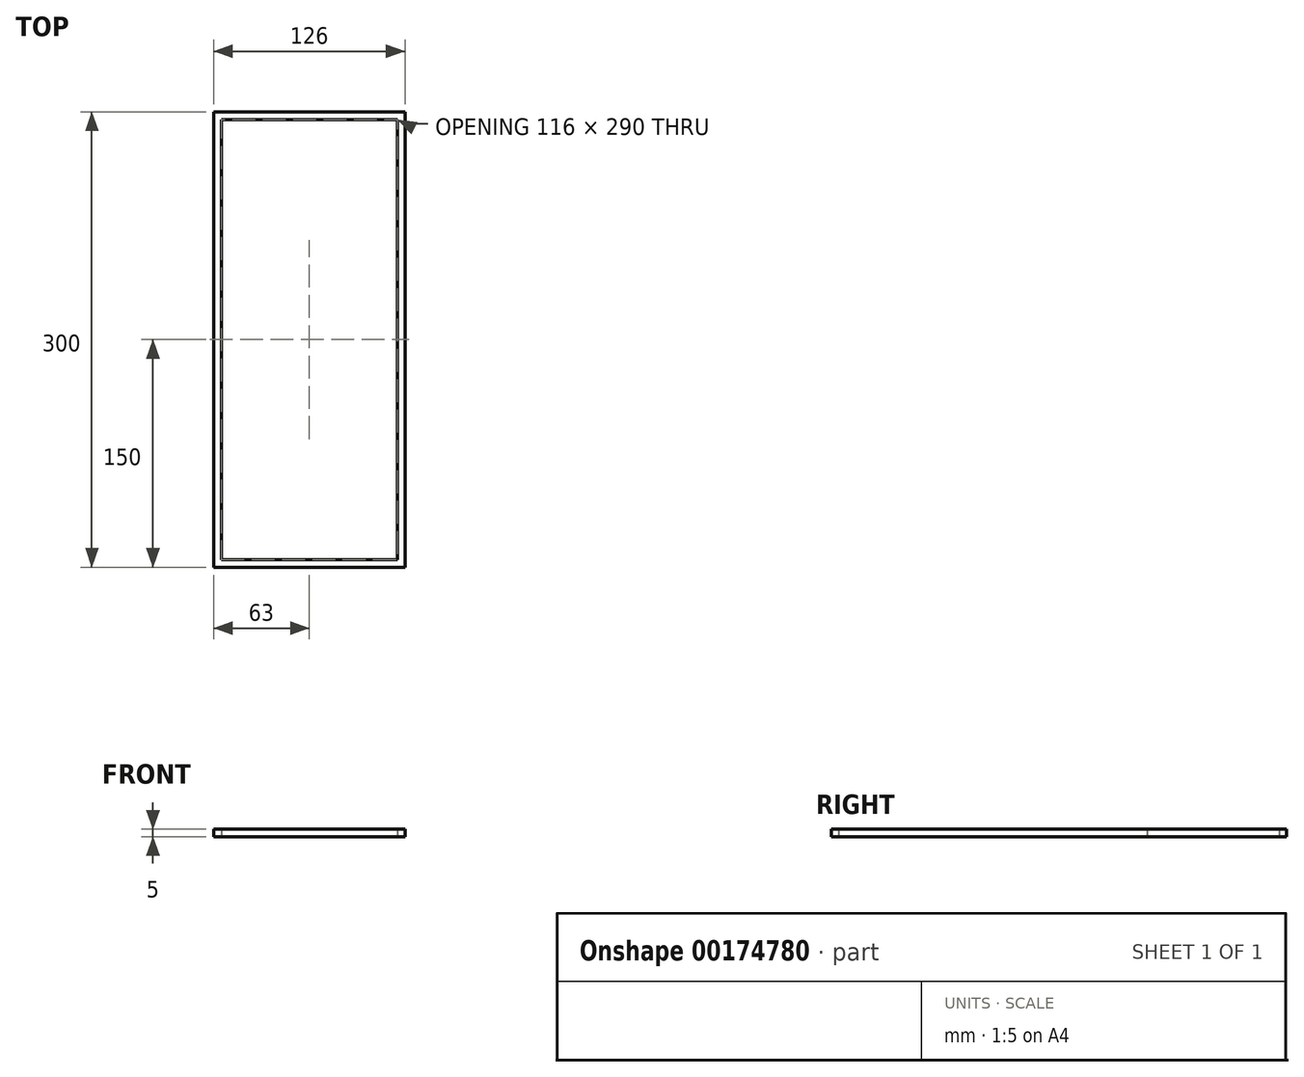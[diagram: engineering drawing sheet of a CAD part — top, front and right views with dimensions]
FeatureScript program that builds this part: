
annotation { "Feature Type Name" : "Feature", "Feature Type Description" : "" }
export const myFeature = defineFeature(function(context is Context, id is Id, definition is map)
    precondition{}
    {
        {
            var Q0;
            Q0=qCreatedBy(makeId("Top.planeOp"),FACE);
            var sketch = newSketch(context, id + "F0", { "sketchPlane" : qUnion([Q0])});
            skLineSegment(sketch, "E0.bottom", {"start": v(0, 0) * mm, "end": v(126, 0) * mm});
            skLineSegment(sketch, "E0.top", {"start": v(0, 300) * mm, "end": v(126, 300) * mm});
            skLineSegment(sketch, "E0.left", {"start": v(0, 0) * mm, "end": v(0, 300) * mm});
            skLineSegment(sketch, "E0.right", {"start": v(126, 0) * mm, "end": v(126, 300) * mm});
            skLineSegment(sketch, "E1.bottom", {"start": v(5, 5) * mm, "end": v(34, 5) * mm});
            skLineSegment(sketch, "E1.top", {"start": v(5, 34) * mm, "end": v(34, 34) * mm});
            skLineSegment(sketch, "E1.left", {"start": v(5, 5) * mm, "end": v(5, 34) * mm});
            skLineSegment(sketch, "E1.right", {"start": v(34, 5) * mm, "end": v(34, 34) * mm});
            skLineSegment(sketch, "E2.0.1.0", {"start": v(5, 63) * mm, "end": v(34, 63) * mm});
            skLineSegment(sketch, "E2.0.1.1", {"start": v(5, 34) * mm, "end": v(5, 63) * mm});
            skLineSegment(sketch, "E2.0.2.0", {"start": v(5, 92) * mm, "end": v(34, 92) * mm});
            skLineSegment(sketch, "E2.0.2.1", {"start": v(5, 63) * mm, "end": v(5, 92) * mm});
            skLineSegment(sketch, "E2.0.3.0", {"start": v(5, 121) * mm, "end": v(34, 121) * mm});
            skLineSegment(sketch, "E2.0.3.1", {"start": v(5, 92) * mm, "end": v(5, 121) * mm});
            skLineSegment(sketch, "E2.0.4.0", {"start": v(5, 150) * mm, "end": v(34, 150) * mm});
            skLineSegment(sketch, "E2.0.4.1", {"start": v(5, 121) * mm, "end": v(5, 150) * mm});
            skLineSegment(sketch, "E2.0.5.0", {"start": v(5, 179) * mm, "end": v(34, 179) * mm});
            skLineSegment(sketch, "E2.0.5.1", {"start": v(5, 150) * mm, "end": v(5, 179) * mm});
            skLineSegment(sketch, "E2.0.6.0", {"start": v(5, 208) * mm, "end": v(34, 208) * mm});
            skLineSegment(sketch, "E2.0.6.1", {"start": v(5, 179) * mm, "end": v(5, 208) * mm});
            skLineSegment(sketch, "E2.0.7.0", {"start": v(5, 237) * mm, "end": v(34, 237) * mm});
            skLineSegment(sketch, "E2.0.7.1", {"start": v(5, 208) * mm, "end": v(5, 237) * mm});
            skLineSegment(sketch, "E2.0.8.0", {"start": v(5, 266) * mm, "end": v(34, 266) * mm});
            skLineSegment(sketch, "E2.0.8.1", {"start": v(5, 237) * mm, "end": v(5, 266) * mm});
            skLineSegment(sketch, "E2.0.9.0", {"start": v(5, 295) * mm, "end": v(34, 295) * mm});
            skLineSegment(sketch, "E2.0.9.1", {"start": v(5, 266) * mm, "end": v(5, 295) * mm});
            skLineSegment(sketch, "E2.1.0.0", {"start": v(34, 34) * mm, "end": v(63, 34) * mm});
            skLineSegment(sketch, "E2.1.1.0", {"start": v(34, 63) * mm, "end": v(63, 63) * mm});
            skLineSegment(sketch, "E2.1.1.1", {"start": v(34, 34) * mm, "end": v(34, 63) * mm});
            skLineSegment(sketch, "E2.1.2.0", {"start": v(34, 92) * mm, "end": v(63, 92) * mm});
            skLineSegment(sketch, "E2.1.2.1", {"start": v(34, 63) * mm, "end": v(34, 92) * mm});
            skLineSegment(sketch, "E2.1.3.0", {"start": v(34, 121) * mm, "end": v(63, 121) * mm});
            skLineSegment(sketch, "E2.1.3.1", {"start": v(34, 92) * mm, "end": v(34, 121) * mm});
            skLineSegment(sketch, "E2.1.4.0", {"start": v(34, 150) * mm, "end": v(63, 150) * mm});
            skLineSegment(sketch, "E2.1.4.1", {"start": v(34, 121) * mm, "end": v(34, 150) * mm});
            skLineSegment(sketch, "E2.1.5.0", {"start": v(34, 179) * mm, "end": v(63, 179) * mm});
            skLineSegment(sketch, "E2.1.5.1", {"start": v(34, 150) * mm, "end": v(34, 179) * mm});
            skLineSegment(sketch, "E2.1.6.0", {"start": v(34, 208) * mm, "end": v(63, 208) * mm});
            skLineSegment(sketch, "E2.1.6.1", {"start": v(34, 179) * mm, "end": v(34, 208) * mm});
            skLineSegment(sketch, "E2.1.7.0", {"start": v(34, 237) * mm, "end": v(63, 237) * mm});
            skLineSegment(sketch, "E2.1.7.1", {"start": v(34, 208) * mm, "end": v(34, 237) * mm});
            skLineSegment(sketch, "E2.1.8.0", {"start": v(34, 266) * mm, "end": v(63, 266) * mm});
            skLineSegment(sketch, "E2.1.8.1", {"start": v(34, 237) * mm, "end": v(34, 266) * mm});
            skLineSegment(sketch, "E2.1.9.0", {"start": v(34, 295) * mm, "end": v(63, 295) * mm});
            skLineSegment(sketch, "E2.1.9.1", {"start": v(34, 266) * mm, "end": v(34, 295) * mm});
            skLineSegment(sketch, "E2.2.0.0", {"start": v(63, 34) * mm, "end": v(92, 34) * mm});
            skLineSegment(sketch, "E2.2.0.1", {"start": v(63, 5) * mm, "end": v(63, 34) * mm});
            skLineSegment(sketch, "E2.2.1.0", {"start": v(63, 63) * mm, "end": v(92, 63) * mm});
            skLineSegment(sketch, "E2.2.1.1", {"start": v(63, 34) * mm, "end": v(63, 63) * mm});
            skLineSegment(sketch, "E2.2.2.0", {"start": v(63, 92) * mm, "end": v(92, 92) * mm});
            skLineSegment(sketch, "E2.2.2.1", {"start": v(63, 63) * mm, "end": v(63, 92) * mm});
            skLineSegment(sketch, "E2.2.3.0", {"start": v(63, 121) * mm, "end": v(92, 121) * mm});
            skLineSegment(sketch, "E2.2.3.1", {"start": v(63, 92) * mm, "end": v(63, 121) * mm});
            skLineSegment(sketch, "E2.2.4.0", {"start": v(63, 150) * mm, "end": v(92, 150) * mm});
            skLineSegment(sketch, "E2.2.4.1", {"start": v(63, 121) * mm, "end": v(63, 150) * mm});
            skLineSegment(sketch, "E2.2.5.0", {"start": v(63, 179) * mm, "end": v(92, 179) * mm});
            skLineSegment(sketch, "E2.2.5.1", {"start": v(63, 150) * mm, "end": v(63, 179) * mm});
            skLineSegment(sketch, "E2.2.6.0", {"start": v(63, 208) * mm, "end": v(92, 208) * mm});
            skLineSegment(sketch, "E2.2.6.1", {"start": v(63, 179) * mm, "end": v(63, 208) * mm});
            skLineSegment(sketch, "E2.2.7.0", {"start": v(63, 237) * mm, "end": v(92, 237) * mm});
            skLineSegment(sketch, "E2.2.7.1", {"start": v(63, 208) * mm, "end": v(63, 237) * mm});
            skLineSegment(sketch, "E2.2.8.0", {"start": v(63, 266) * mm, "end": v(92, 266) * mm});
            skLineSegment(sketch, "E2.2.8.1", {"start": v(63, 237) * mm, "end": v(63, 266) * mm});
            skLineSegment(sketch, "E2.2.9.0", {"start": v(63, 295) * mm, "end": v(92, 295) * mm});
            skLineSegment(sketch, "E2.2.9.1", {"start": v(63, 266) * mm, "end": v(63, 295) * mm});
            skLineSegment(sketch, "E2.3.0.0", {"start": v(92, 34) * mm, "end": v(121, 34) * mm});
            skLineSegment(sketch, "E2.3.0.1", {"start": v(92, 5) * mm, "end": v(92, 34) * mm});
            skLineSegment(sketch, "E2.3.1.0", {"start": v(92, 63) * mm, "end": v(121, 63) * mm});
            skLineSegment(sketch, "E2.3.1.1", {"start": v(92, 34) * mm, "end": v(92, 63) * mm});
            skLineSegment(sketch, "E2.3.2.0", {"start": v(92, 92) * mm, "end": v(121, 92) * mm});
            skLineSegment(sketch, "E2.3.2.1", {"start": v(92, 63) * mm, "end": v(92, 92) * mm});
            skLineSegment(sketch, "E2.3.3.0", {"start": v(92, 121) * mm, "end": v(121, 121) * mm});
            skLineSegment(sketch, "E2.3.3.1", {"start": v(92, 92) * mm, "end": v(92, 121) * mm});
            skLineSegment(sketch, "E2.3.4.0", {"start": v(92, 150) * mm, "end": v(121, 150) * mm});
            skLineSegment(sketch, "E2.3.4.1", {"start": v(92, 121) * mm, "end": v(92, 150) * mm});
            skLineSegment(sketch, "E2.3.5.0", {"start": v(92, 179) * mm, "end": v(121, 179) * mm});
            skLineSegment(sketch, "E2.3.5.1", {"start": v(92, 150) * mm, "end": v(92, 179) * mm});
            skLineSegment(sketch, "E2.3.6.0", {"start": v(92, 208) * mm, "end": v(121, 208) * mm});
            skLineSegment(sketch, "E2.3.6.1", {"start": v(92, 179) * mm, "end": v(92, 208) * mm});
            skLineSegment(sketch, "E2.3.7.0", {"start": v(92, 237) * mm, "end": v(121, 237) * mm});
            skLineSegment(sketch, "E2.3.7.1", {"start": v(92, 208) * mm, "end": v(92, 237) * mm});
            skLineSegment(sketch, "E2.3.8.0", {"start": v(92, 266) * mm, "end": v(121, 266) * mm});
            skLineSegment(sketch, "E2.3.8.1", {"start": v(92, 237) * mm, "end": v(92, 266) * mm});
            skLineSegment(sketch, "E2.3.9.0", {"start": v(92, 295) * mm, "end": v(121, 295) * mm});
            skLineSegment(sketch, "E2.3.9.1", {"start": v(92, 266) * mm, "end": v(92, 295) * mm});
            skLineSegment(sketch, "E2.direction1", {"start": v(5, 34) * mm, "end": v(34, 34) * mm, "construction": true});
            skLineSegment(sketch, "E2.direction2", {"start": v(5, 34) * mm, "end": v(5, 63) * mm, "construction": true});
            skLineSegment(sketch, "E3", {"start": v(34, 5) * mm, "end": v(63, 5) * mm});
            skLineSegment(sketch, "E4", {"start": v(92, 5) * mm, "end": v(63, 5) * mm});
            skLineSegment(sketch, "E5", {"start": v(121, 295) * mm, "end": v(121, 266) * mm});
            skLineSegment(sketch, "E6", {"start": v(121, 266) * mm, "end": v(121, 237) * mm});
            skLineSegment(sketch, "E7", {"start": v(121, 237) * mm, "end": v(121, 208) * mm});
            skLineSegment(sketch, "E8", {"start": v(120.96, 208.84) * mm, "end": v(121, 179) * mm});
            skLineSegment(sketch, "E9", {"start": v(121, 179) * mm, "end": v(121, 150) * mm});
            skLineSegment(sketch, "E10", {"start": v(121, 150) * mm, "end": v(121, 121) * mm});
            skLineSegment(sketch, "E11", {"start": v(121, 121) * mm, "end": v(121, 92) * mm});
            skLineSegment(sketch, "E12", {"start": v(121, 92) * mm, "end": v(121, 63) * mm});
            skLineSegment(sketch, "E13", {"start": v(121, 63) * mm, "end": v(121, 34) * mm});
            skLineSegment(sketch, "E14", {"start": v(92, 5) * mm, "end": v(121, 5) * mm});
            skLineSegment(sketch, "E15", {"start": v(121, 34) * mm, "end": v(121, 5) * mm});
            skSolve(sketch);
        }
        {
            var Q0;
            Q0=makeQuery(id+"F0.imprint","IMPRINT",FACE,{"disambiguationData":[TD([[makeQuery(id+"F0.imprint","IMPRINT",EDGE,{"derivedFrom":sQuery(id+"F0.wireOp",EDGE,"E0.bottom")}),1.0]])]});
            extrude(context, id + "F1", {"entities" : qUnion([Q0]), "depth" : 5 * mm});
        }
    });
